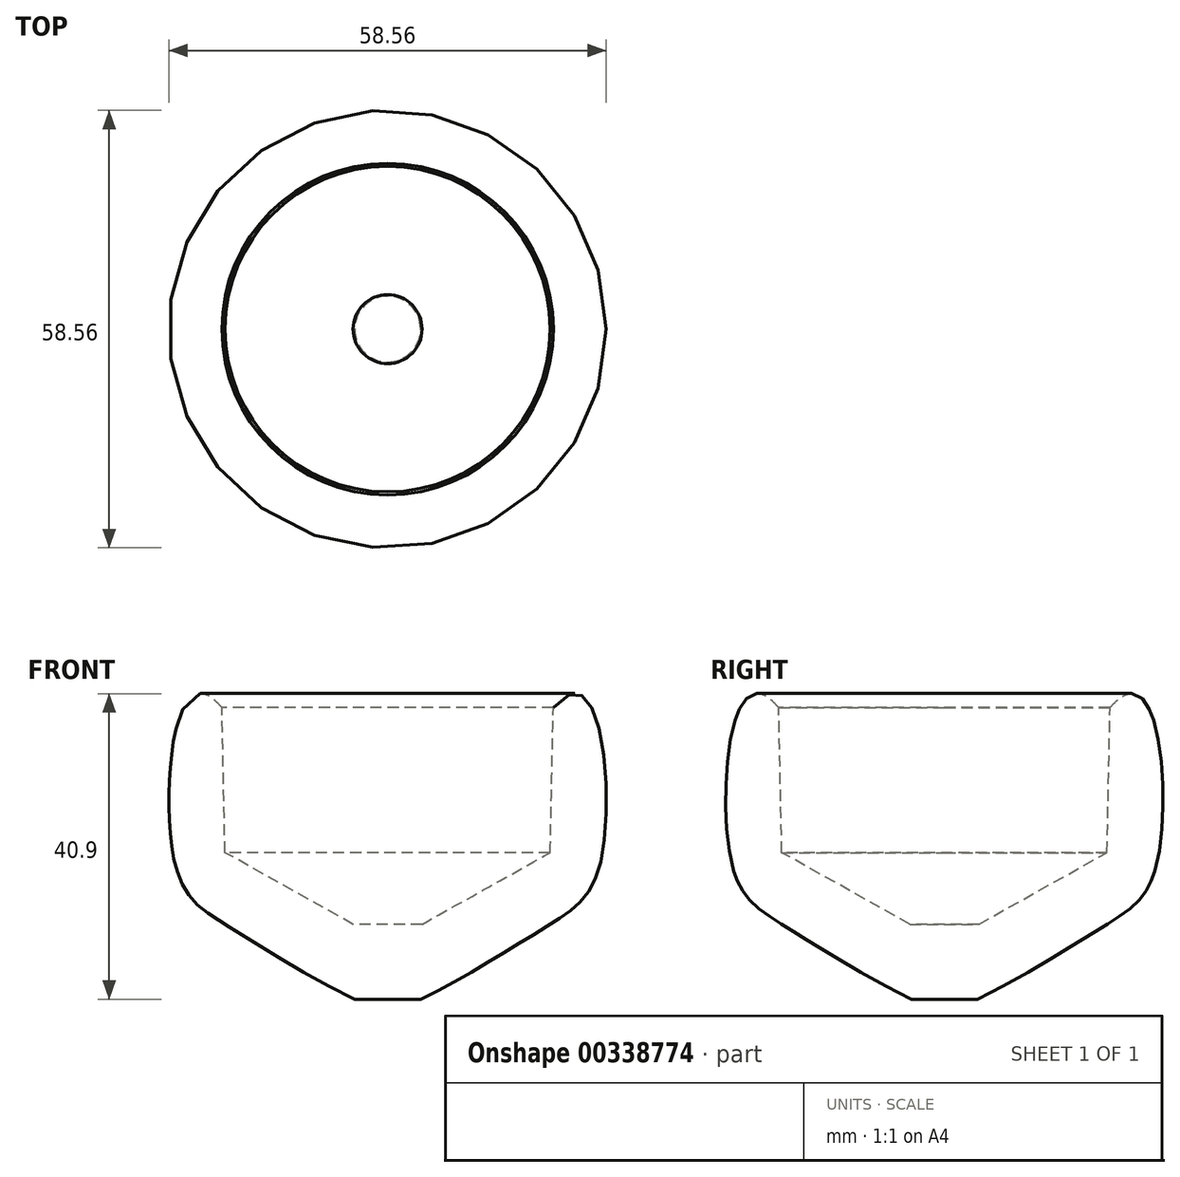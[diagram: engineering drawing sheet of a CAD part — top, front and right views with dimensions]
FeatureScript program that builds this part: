
annotation { "Feature Type Name" : "Feature", "Feature Type Description" : "" }
export const myFeature = defineFeature(function(context is Context, id is Id, definition is map)
    precondition{}
    {
        {
            var Q0;
            Q0=qCreatedBy(makeId("Front.planeOp"),FACE);
            var sketch = newSketch(context, id + "F0", { "sketchPlane" : qUnion([Q0])});
            skFitSpline(sketch, "E0", {"points": [v(-13.47, 0) * mm, v(-30.83, 10.03) * mm, v(-38.04, 21.1) * mm, v(-31.24, 39) * mm], "startDerivative": vector(-52.12, 25.18) * mm, "endDerivative": vector(54.17, -64.54) * mm});
            skLineSegment(sketch, "E1", {"start": v(-31.24, 39) * mm, "end": v(-30.83, 19.63) * mm});
            skLineSegment(sketch, "E2", {"start": v(-30.83, 19.63) * mm, "end": v(-13.66, 10.03) * mm});
            skLineSegment(sketch, "E3", {"start": v(-13.66, 10.03) * mm, "end": v(-9.05, 10.03) * mm});
            skLineSegment(sketch, "E4", {"start": v(-9.05, 10.03) * mm, "end": v(-9.05, 0) * mm});
            skLineSegment(sketch, "E5", {"start": v(-9.05, 0) * mm, "end": v(-13.47, 0) * mm});
            skSolve(sketch);
        }
        {
            var Q0;
            Q0=makeQuery(id+"F0.imprint","IMPRINT",FACE,{"disambiguationData":[TD([[makeQuery(id+"F0.imprint","IMPRINT",EDGE,{"derivedFrom":sQuery(id+"F0.wireOp",EDGE,"E0")}),-1.0]])]});
            var Q1;
            Q1=sQuery(id+"F0.wireOp",EDGE,"E4");
            revolve(context, id + "F1", {"entities" : qUnion([Q0]), "axis" : qUnion([Q1]), "revolveType" : RevolveType.FULL});
        }
    });
